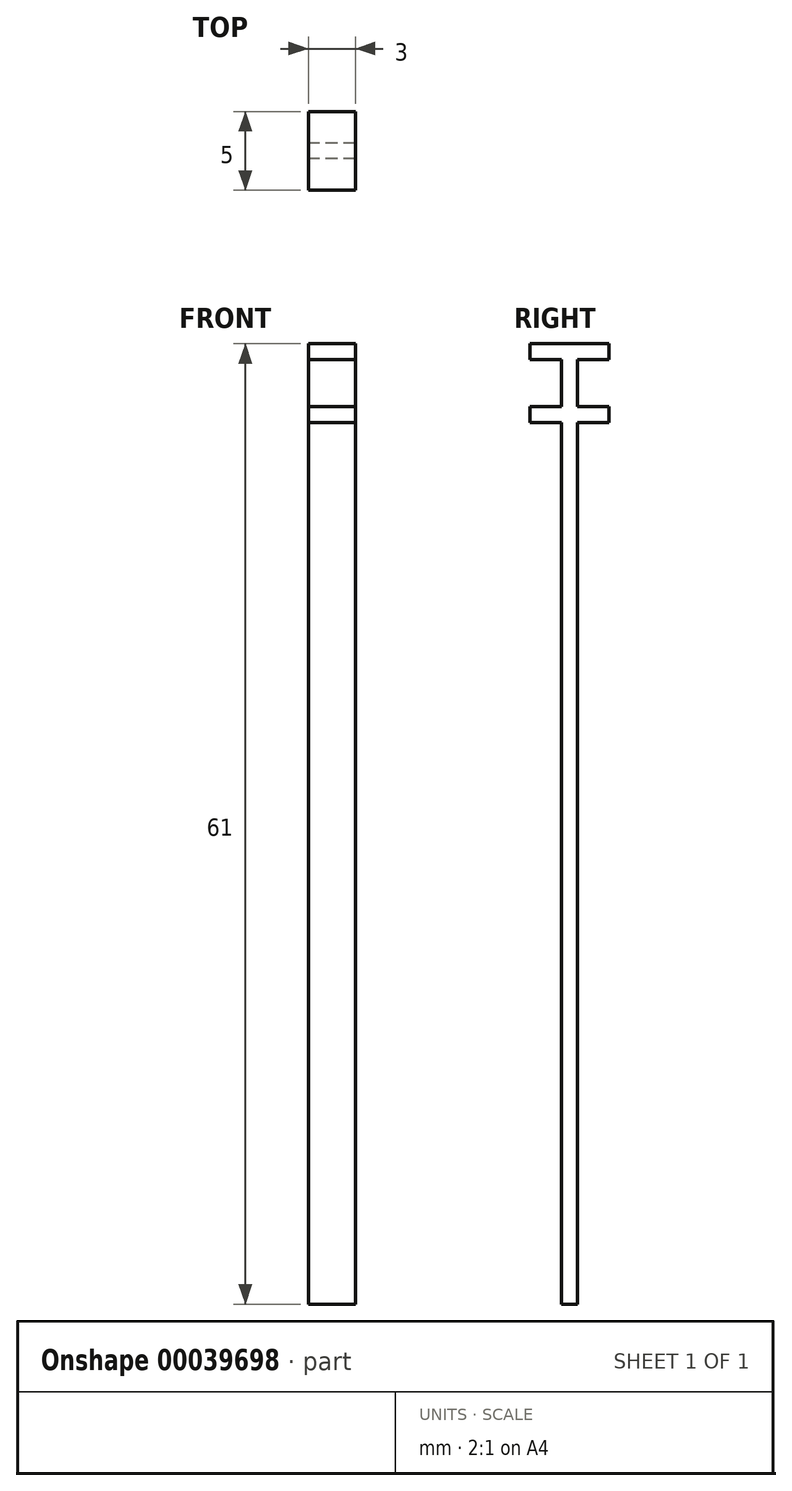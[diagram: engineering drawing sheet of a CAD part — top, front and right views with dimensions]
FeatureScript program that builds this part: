
annotation { "Feature Type Name" : "Feature", "Feature Type Description" : "" }
export const myFeature = defineFeature(function(context is Context, id is Id, definition is map)
    precondition{}
    {
        {
            var Q0;
            Q0=qCreatedBy(makeId("Right.planeOp"),FACE);
            var sketch = newSketch(context, id + "F0", { "sketchPlane" : qUnion([Q0])});
            skLineSegment(sketch, "E0", {"start": v(-2.5, 0) * mm, "end": v(2.5, 0) * mm});
            skLineSegment(sketch, "E1", {"start": v(2.5, 0) * mm, "end": v(2.5, -1) * mm});
            skLineSegment(sketch, "E2", {"start": v(2.5, -1) * mm, "end": v(0.5, -1) * mm});
            skLineSegment(sketch, "E3", {"start": v(0.5, -1) * mm, "end": v(0.5, -4) * mm});
            skLineSegment(sketch, "E4", {"start": v(0.5, -61) * mm, "end": v(-0.5, -61) * mm});
            skLineSegment(sketch, "E5", {"start": v(-0.5, -61) * mm, "end": v(-0.5, -5) * mm});
            skLineSegment(sketch, "E6", {"start": v(-0.5, -1) * mm, "end": v(-2.5, -1) * mm});
            skLineSegment(sketch, "E7", {"start": v(-2.5, -1) * mm, "end": v(-2.5, 0) * mm});
            skLineSegment(sketch, "E8", {"start": v(-0.5, -4) * mm, "end": v(-2.5, -4) * mm});
            skLineSegment(sketch, "E9", {"start": v(-2.5, -4) * mm, "end": v(-2.5, -5) * mm});
            skLineSegment(sketch, "E10", {"start": v(-2.5, -5) * mm, "end": v(-0.5, -5) * mm});
            skLineSegment(sketch, "E11.trimOffspring", {"start": v(-0.5, -4) * mm, "end": v(-0.5, -1) * mm});
            skLineSegment(sketch, "E12", {"start": v(0.5, -4) * mm, "end": v(2.5, -4) * mm});
            skLineSegment(sketch, "E13", {"start": v(2.5, -4) * mm, "end": v(2.5, -5) * mm});
            skLineSegment(sketch, "E14", {"start": v(2.5, -5) * mm, "end": v(0.5, -5) * mm});
            skLineSegment(sketch, "E15.trimOffspring", {"start": v(0.5, -5) * mm, "end": v(0.5, -61) * mm});
            skSolve(sketch);
        }
        {
            var Q0;
            Q0=makeQuery(id+"F0.imprint","IMPRINT",FACE,{"disambiguationData":[TD([[makeQuery(id+"F0.imprint","IMPRINT",EDGE,{"derivedFrom":sQuery(id+"F0.wireOp",EDGE,"E0")}),-1.0]])]});
            extrude(context, id + "F1", {"entities" : qUnion([Q0]), "depth" : 3 * mm});
        }
    });
